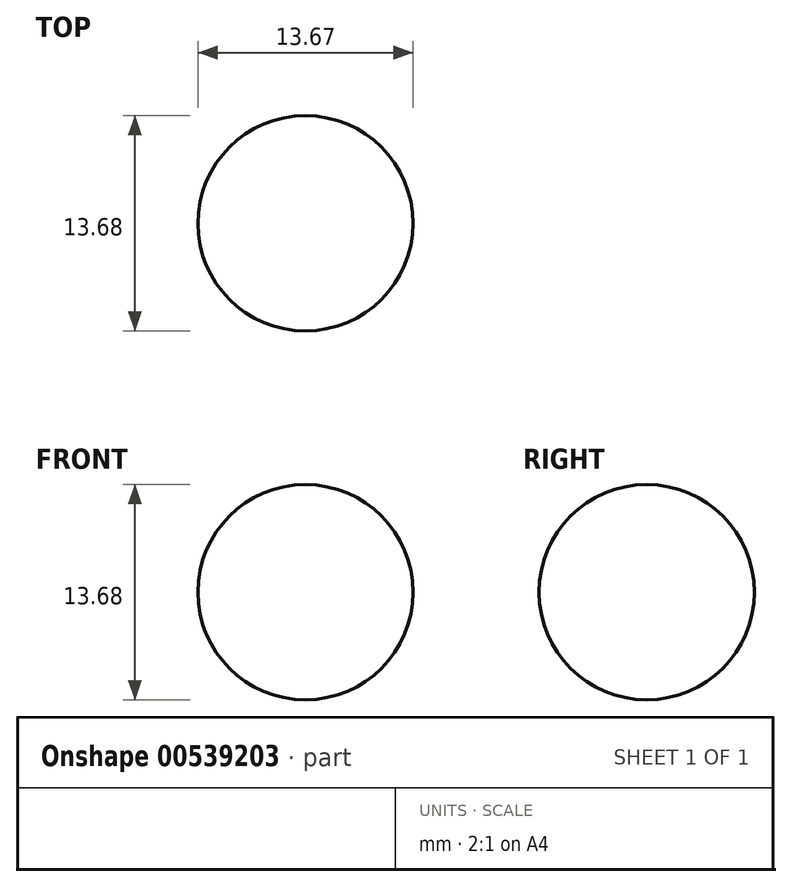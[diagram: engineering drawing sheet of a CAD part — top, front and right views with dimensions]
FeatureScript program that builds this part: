
annotation { "Feature Type Name" : "Feature", "Feature Type Description" : "" }
export const myFeature = defineFeature(function(context is Context, id is Id, definition is map)
    precondition{}
    {
        {
            var Q0;
            Q0=qCreatedBy(makeId("Front.planeOp"),FACE);
            var sketch = newSketch(context, id + "F0", { "sketchPlane" : qUnion([Q0])});
            skArc(sketch, "E0", {"start": v(-45.66, 0) * mm, "mid": v(-38.82, -6.84) * mm, "end": v(-31.99, 0) * mm});
            skLineSegment(sketch, "E1", {"start": v(-45.66, 0) * mm, "end": v(-31.99, 0) * mm});
            skLineSegment(sketch, "E2", {"start": v(-59.58, 0) * mm, "end": v(-21.04, 0) * mm, "construction": true});
            skSolve(sketch);
        }
        {
            var Q0;
            Q0=makeQuery(id+"F0.imprint","IMPRINT",FACE,{"disambiguationData":[TD([[makeQuery(id+"F0.imprint","IMPRINT",EDGE,{"derivedFrom":sQuery(id+"F0.wireOp",EDGE,"E0")}),1.0]])]});
            var Q1;
            Q1=sQuery(id+"F0.wireOp",EDGE,"E2");
            revolve(context, id + "F1", {"entities" : qUnion([Q0]), "axis" : qUnion([Q1]), "revolveType" : RevolveType.FULL});
        }
    });
